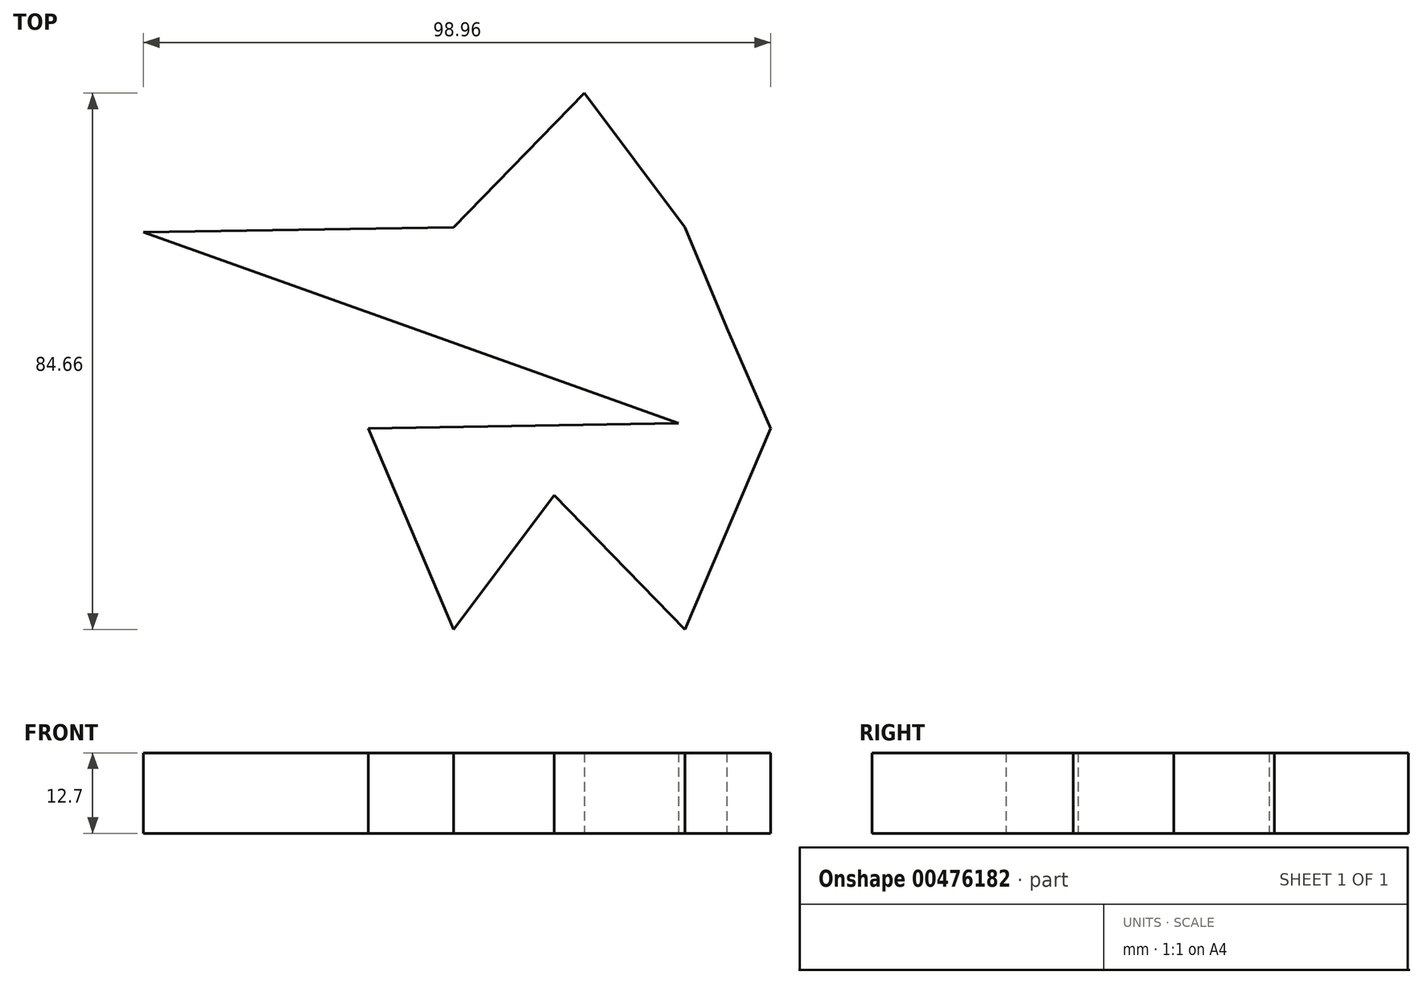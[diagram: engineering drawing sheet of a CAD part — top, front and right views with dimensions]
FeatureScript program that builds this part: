
annotation { "Feature Type Name" : "Feature", "Feature Type Description" : "" }
export const myFeature = defineFeature(function(context is Context, id is Id, definition is map)
    precondition{}
    {
        {
            var Q0;
            Q0=qCreatedBy(makeId("Top.planeOp"),FACE);
            var sketch = newSketch(context, id + "F0", { "sketchPlane" : qUnion([Q0])});
            skLineSegment(sketch, "E0", {"start": v(35.98, 21.17) * mm, "end": v(42.6, 5.3) * mm});
            skLineSegment(sketch, "E1", {"start": v(42.6, 5.3) * mm, "end": v(49.48, -10.58) * mm});
            skLineSegment(sketch, "E2", {"start": v(49.48, -10.58) * mm, "end": v(35.98, -42.33) * mm});
            skLineSegment(sketch, "E3", {"start": v(-0.53, -42.33) * mm, "end": v(-14.02, -10.58) * mm});
            skLineSegment(sketch, "E4", {"start": v(-0.53, 21.17) * mm, "end": v(20.1, 42.33) * mm});
            skLineSegment(sketch, "E5", {"start": v(20.1, 42.33) * mm, "end": v(35.98, 21.17) * mm});
            skLineSegment(sketch, "E6", {"start": v(35.98, -42.33) * mm, "end": v(15.35, -21.17) * mm});
            skLineSegment(sketch, "E7", {"start": v(15.35, -21.17) * mm, "end": v(-0.53, -42.33) * mm});
            skLineSegment(sketch, "E8", {"start": v(-14.02, -10.58) * mm, "end": v(34.93, -9.79) * mm});
            skLineSegment(sketch, "E9", {"start": v(34.93, -9.79) * mm, "end": v(-7.14, 5.3) * mm});
            skLineSegment(sketch, "E10", {"start": v(-7.14, 5.3) * mm, "end": v(-49.48, 20.37) * mm});
            skLineSegment(sketch, "E11", {"start": v(-49.48, 20.37) * mm, "end": v(-0.53, 21.17) * mm});
            skSolve(sketch);
        }
        {
            var Q0;
            Q0=makeQuery(id+"F0.imprint","IMPRINT",FACE,{"disambiguationData":[TD([[makeQuery(id+"F0.imprint","IMPRINT",EDGE,{"derivedFrom":sQuery(id+"F0.wireOp",EDGE,"E4")}),-1.0]])]});
            var Q1;
            Q1=sQuery(id+"F0.wireOp",EDGE,"E8");
            var Q2;
            Q2=sQuery(id+"F0.wireOp",EDGE,"E3");
            var Q3;
            Q3=sQuery(id+"F0.wireOp",EDGE,"E7");
            var Q4;
            Q4=sQuery(id+"F0.wireOp",EDGE,"E6");
            var Q5;
            Q5=sQuery(id+"F0.wireOp",EDGE,"E2");
            var Q6;
            Q6=sQuery(id+"F0.wireOp",EDGE,"E1");
            var Q7;
            Q7=sQuery(id+"F0.wireOp",EDGE,"E0");
            var Q8;
            Q8=sQuery(id+"F0.wireOp",EDGE,"E5");
            var Q9;
            Q9=sQuery(id+"F0.wireOp",EDGE,"E4");
            var Q10;
            Q10=sQuery(id+"F0.wireOp",EDGE,"E11");
            var Q11;
            Q11=sQuery(id+"F0.wireOp",EDGE,"E10");
            var Q12;
            Q12=sQuery(id+"F0.wireOp",EDGE,"E9");
            extrude(context, id + "F1", {"entities" : qUnion([Q0]), "surfaceEntities" : qUnion([Q1, Q2, Q3, Q4, Q5, Q6, Q7, Q8, Q9, Q10, Q11, Q12]), "depth" : 12.7 * mm});
        }
    });
